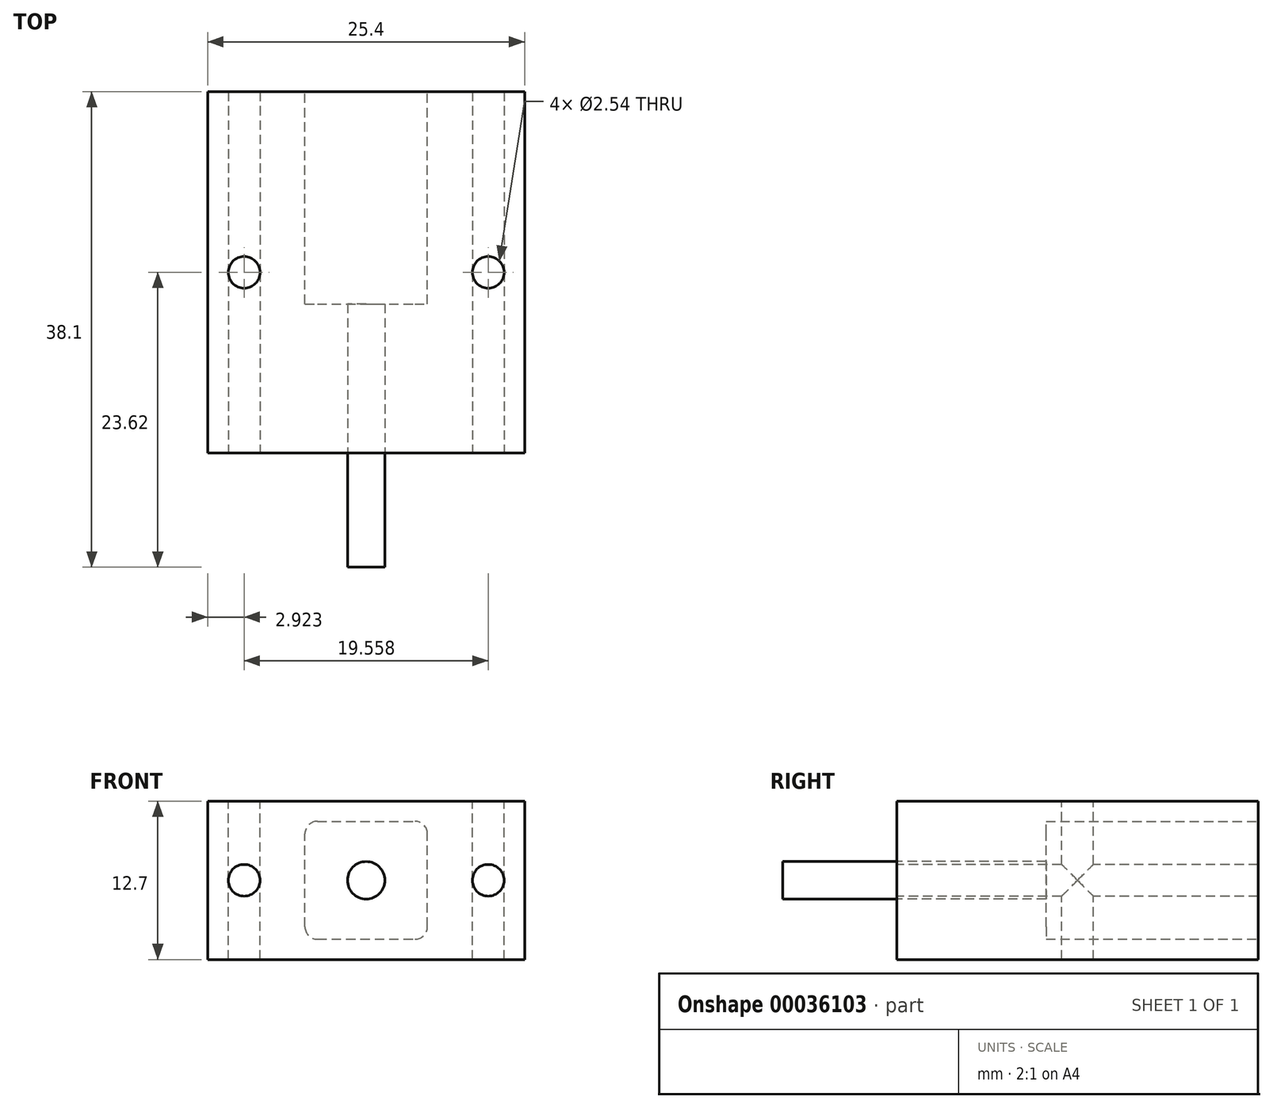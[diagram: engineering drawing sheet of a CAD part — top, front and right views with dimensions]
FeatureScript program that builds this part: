
annotation { "Feature Type Name" : "Feature", "Feature Type Description" : "" }
export const myFeature = defineFeature(function(context is Context, id is Id, definition is map)
    precondition{}
    {
        {
            var Q0;
            Q0=qCreatedBy(makeId("Top.planeOp"),FACE);
            var sketch = newSketch(context, id + "F0", { "sketchPlane" : qUnion([Q0])});
            skLineSegment(sketch, "E0.bottom", {"start": v(-12.47, 12.97) * mm, "end": v(12.93, 12.97) * mm});
            skLineSegment(sketch, "E0.top", {"start": v(-12.47, -15.99) * mm, "end": v(12.93, -15.99) * mm});
            skLineSegment(sketch, "E0.left", {"start": v(-12.47, 12.97) * mm, "end": v(-12.47, -15.99) * mm});
            skLineSegment(sketch, "E0.right", {"start": v(12.93, 12.97) * mm, "end": v(12.93, -15.99) * mm});
            skSolve(sketch);
        }
        {
            var Q0;
            Q0=makeQuery(id+"F0.imprint","IMPRINT",FACE,{"disambiguationData":[TD([[makeQuery(id+"F0.imprint","IMPRINT",EDGE,{"derivedFrom":sQuery(id+"F0.wireOp",EDGE,"E0.bottom")}),-1.0]])]});
            extrude(context, id + "F1", {"entities" : qUnion([Q0]), "depth" : 12.7 * mm});
        }
        {
            var Q0;
            Q0=makeQuery(id+"F1.opExtrude","SWEPT_FACE",FACE,{"disambiguationData":[OSD([sQuery(id+"F0.wireOp",EDGE,"E0.top")])]});
            var sketch = newSketch(context, id + "F2", { "sketchPlane" : qUnion([Q0])});
            skPoint(sketch, "E1", {"position": v(-12.47, 6.35) * mm});
            skPoint(sketch, "E2", {"position": v(12.93, 6.35) * mm});
            skLineSegment(sketch, "E3", {"start": v(-12.47, 6.35) * mm, "end": v(12.93, 6.35) * mm, "construction": true});
            skPoint(sketch, "E4", {"position": v(0.23, 6.35) * mm});
            skLineSegment(sketch, "E5", {"start": v(0.23, 6.35) * mm, "end": v(-9.55, 6.35) * mm});
            skLineSegment(sketch, "E6", {"start": v(0.23, 6.35) * mm, "end": v(10.01, 6.35) * mm});
            skCircle(sketch, "E7", {"center": v(0.23, 6.35) * mm, "radius": 1.5 * mm});
            skSolve(sketch);
        }
        {
            var Q0;
            Q0=sQuery(id+"F2.wireOp",VERTEX,"E5.end");
            var Q1;
            Q1=sQuery(id+"F2.wireOp",VERTEX,"E6.end");
            var Q2;
            Q2=makeQuery(id+"F1.opExtrude","SWEPT_BODY",BODY,{"disambiguationData":[OSD([sQuery(id+"F0.wireOp",EDGE,"E0.bottom"),sQuery(id+"F0.wireOp",EDGE,"E0.top"),sQuery(id+"F0.wireOp",EDGE,"E0.left"),sQuery(id+"F0.wireOp",EDGE,"E0.right")])]});
            hole(context, id + "F3", {"style" : HoleStyle.SIMPLE, "holeDiameter" : 2.54 * mm, "endStyle" : HoleEndStyle.THROUGH, "locations" : qUnion([Q0, Q1]), "scope" : qUnion([Q2])});
        }
        {
            var Q0;
            Q0=sQuery(id+"F2.wireOp",VERTEX,"E4");
            var Q1;
            Q1=makeQuery(id+"F1.opExtrude","SWEPT_BODY",BODY,{"disambiguationData":[OSD([sQuery(id+"F0.wireOp",EDGE,"E0.bottom"),sQuery(id+"F0.wireOp",EDGE,"E0.top"),sQuery(id+"F0.wireOp",EDGE,"E0.left"),sQuery(id+"F0.wireOp",EDGE,"E0.right")])]});
            hole(context, id + "F4", {"style" : HoleStyle.SIMPLE, "holeDiameter" : 3 * mm, "endStyle" : HoleEndStyle.THROUGH, "locations" : qUnion([Q0]), "scope" : qUnion([Q1])});
        }
        {
            var Q0;
            Q0=makeQuery(id+"F1.opExtrude","CAP_FACE",FACE,{"disambiguationData":[OSD([sQuery(id+"F0.wireOp",EDGE,"E0.bottom"),sQuery(id+"F0.wireOp",EDGE,"E0.top"),sQuery(id+"F0.wireOp",EDGE,"E0.left"),sQuery(id+"F0.wireOp",EDGE,"E0.right")])],"isStart":false});
            var sketch = newSketch(context, id + "F5", { "sketchPlane" : qUnion([Q0])});
            skLineSegment(sketch, "E8", {"start": v(-12.47, -1.51) * mm, "end": v(12.93, -1.51) * mm, "construction": true});
            skPoint(sketch, "E9", {"position": v(0.23, -1.51) * mm});
            skLineSegment(sketch, "E10", {"start": v(0.23, -1.51) * mm, "end": v(-9.55, -1.51) * mm});
            skLineSegment(sketch, "E11", {"start": v(0.23, -1.51) * mm, "end": v(10.01, -1.51) * mm});
            skSolve(sketch);
        }
        {
            var Q0;
            Q0=sQuery(id+"F5.wireOp",VERTEX,"E10.end");
            var Q1;
            Q1=sQuery(id+"F5.wireOp",VERTEX,"E11.end");
            var Q2;
            Q2=makeQuery(id+"F1.opExtrude","SWEPT_BODY",BODY,{"disambiguationData":[OSD([sQuery(id+"F0.wireOp",EDGE,"E0.bottom"),sQuery(id+"F0.wireOp",EDGE,"E0.top"),sQuery(id+"F0.wireOp",EDGE,"E0.left"),sQuery(id+"F0.wireOp",EDGE,"E0.right")])]});
            hole(context, id + "F6", {"style" : HoleStyle.SIMPLE, "holeDiameter" : 2.54 * mm, "endStyle" : HoleEndStyle.THROUGH, "locations" : qUnion([Q0, Q1]), "scope" : qUnion([Q2])});
        }
        {
            var Q0;
            Q0 = qSketchRegion(id + "F2", true);
            extrude(context, id + "F7", {"entities" : qUnion([Q0]), "depth" : 9.14 * mm});
        }
        {
            var Q0;
            Q0=makeQuery(id+"F1.opExtrude","SWEPT_FACE",FACE,{"disambiguationData":[OSD([sQuery(id+"F0.wireOp",EDGE,"E0.bottom")])]});
            var sketch = newSketch(context, id + "F8", { "sketchPlane" : qUnion([Q0])});
            skLineSegment(sketch, "E12.rect.bottom", {"start": v(3.68, 1.63) * mm, "end": v(-4.14, 1.63) * mm});
            skLineSegment(sketch, "E12.rect.top", {"start": v(3.68, 11.07) * mm, "end": v(-4.14, 11.07) * mm});
            skLineSegment(sketch, "E12.rect.left", {"start": v(4.68, 2.63) * mm, "end": v(4.68, 10.07) * mm});
            skLineSegment(sketch, "E12.rect.right", {"start": v(-5.14, 2.63) * mm, "end": v(-5.14, 10.07) * mm});
            skPoint(sketch, "E12.rect.middle", {"position": v(-0.23, 6.35) * mm});
            skPoint(sketch, "E13.visualSharp", {"position": v(-5.14, 11.07) * mm});
            skArc(sketch, "E13.filletArc", {"start": v(-4.14, 11.07) * mm, "mid": v(-4.85, 10.78) * mm, "end": v(-5.14, 10.07) * mm});
            skPoint(sketch, "E14.visualSharp", {"position": v(4.68, 11.07) * mm});
            skArc(sketch, "E14.filletArc", {"start": v(4.68, 10.07) * mm, "mid": v(4.38, 10.78) * mm, "end": v(3.68, 11.07) * mm});
            skPoint(sketch, "E15.visualSharp", {"position": v(4.68, 1.63) * mm});
            skArc(sketch, "E15.filletArc", {"start": v(3.68, 1.63) * mm, "mid": v(4.38, 1.92) * mm, "end": v(4.68, 2.63) * mm});
            skPoint(sketch, "E16.visualSharp", {"position": v(-5.14, 1.63) * mm});
            skArc(sketch, "E16.filletArc", {"start": v(-5.14, 2.63) * mm, "mid": v(-4.85, 1.92) * mm, "end": v(-4.14, 1.63) * mm});
            skSolve(sketch);
        }
        {
            var Q0;
            Q0=makeQuery(id+"F8.imprint","IMPRINT",FACE,{"disambiguationData":[TD([[makeQuery(id+"F8.imprint","IMPRINT",EDGE,{"derivedFrom":sQuery(id+"F8.wireOp",EDGE,"E12.rect.bottom")}),-1.0]])]});
            extrude(context, id + "F9", {"entities" : qUnion([Q0]), "operationType" : NewBodyOperationType.REMOVE, "oppositeDirection" : true, "depth" : 17 * mm});
        }
    });
